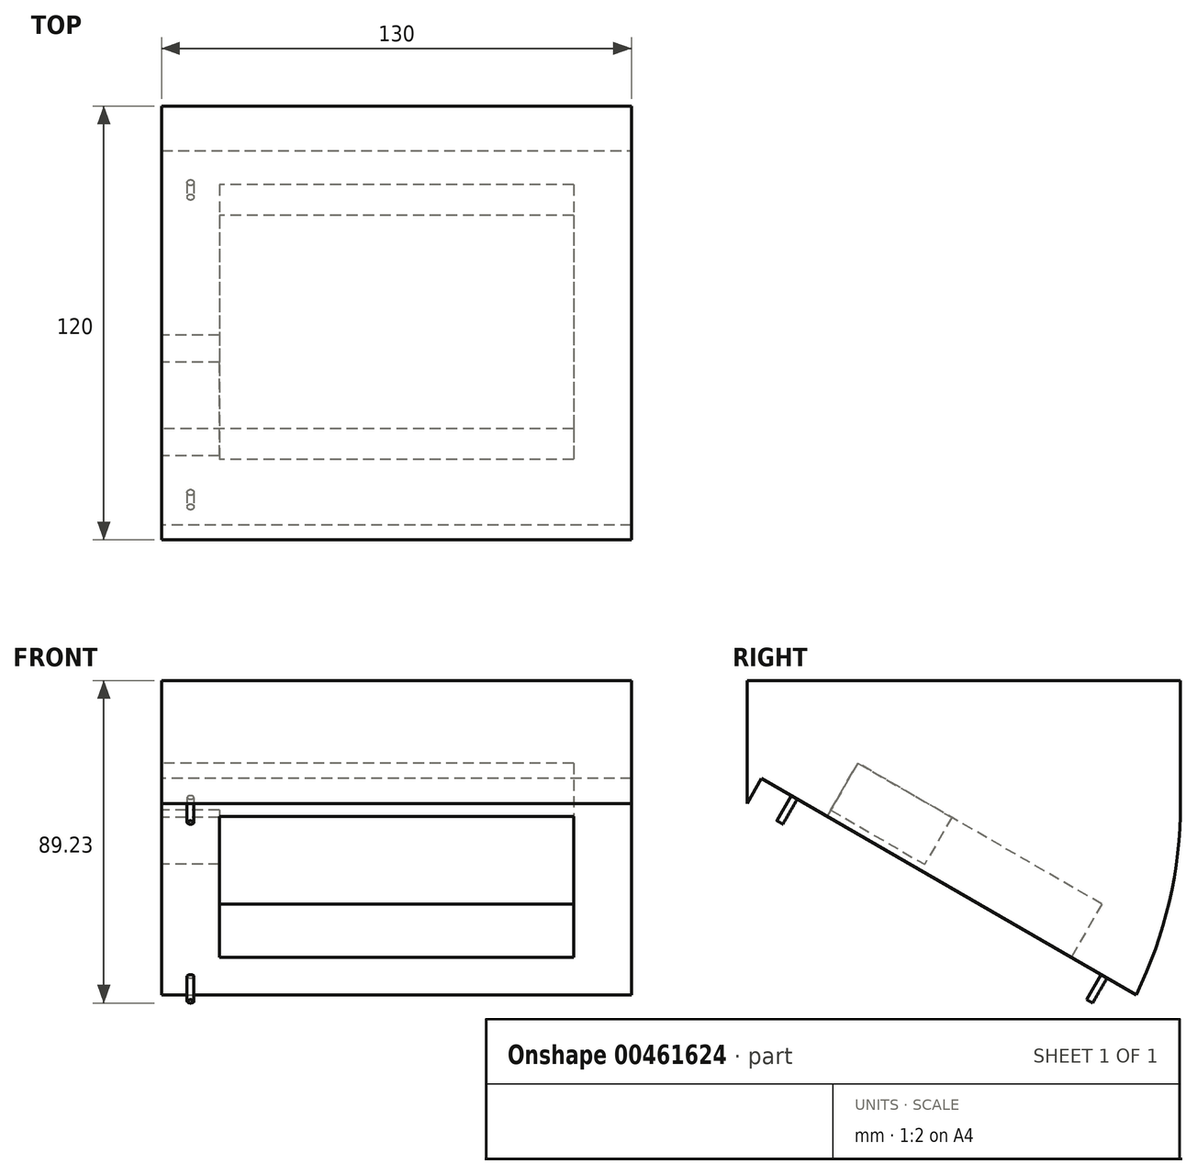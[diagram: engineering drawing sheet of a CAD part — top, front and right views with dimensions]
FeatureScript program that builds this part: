
annotation { "Feature Type Name" : "Feature", "Feature Type Description" : "" }
export const myFeature = defineFeature(function(context is Context, id is Id, definition is map)
    precondition{}
    {
        {
            var Q0;
            Q0=qCreatedBy(makeId("Top.planeOp"),FACE);
            var sketch = newSketch(context, id + "F0", { "sketchPlane" : qUnion([Q0])});
            skLineSegment(sketch, "E0.bottom", {"start": v(65, 60) * mm, "end": v(-65, 60) * mm});
            skLineSegment(sketch, "E0.top", {"start": v(65, -60) * mm, "end": v(-65, -60) * mm});
            skLineSegment(sketch, "E0.left", {"start": v(65, 60) * mm, "end": v(65, -60) * mm});
            skLineSegment(sketch, "E0.right", {"start": v(-65, 60) * mm, "end": v(-65, -60) * mm});
            skPoint(sketch, "E0.middle", {"position": v(0, 0) * mm});
            skSolve(sketch);
        }
        {
            var Q0;
            Q0=makeQuery(id+"F0.imprint","IMPRINT",FACE,{"disambiguationData":[TD([[makeQuery(id+"F0.imprint","IMPRINT",EDGE,{"derivedFrom":sQuery(id+"F0.wireOp",EDGE,"E0.bottom")}),1.0]])]});
            extrude(context, id + "F1", {"entities" : qUnion([Q0]), "depth" : 34 * mm, "offsetDistance" : 25 * mm});
        }
        {
            var Q0;
            Q0=makeQuery(id+"F0.imprint","IMPRINT",FACE,{"disambiguationData":[TD([[makeQuery(id+"F0.imprint","IMPRINT",EDGE,{"derivedFrom":sQuery(id+"F0.wireOp",EDGE,"E0.bottom")}),1.0]])]});
            var Q1;
            Q1=sQuery(id+"F0.wireOp",EDGE,"E0.top");
            revolve(context, id + "F2", {"operationType" : NewBodyOperationType.ADD, "entities" : qUnion([Q0]), "axis" : qUnion([Q1]), "revolveType" : RevolveType.ONE_DIRECTION, "angle" : 30 * degree});
        }
        {
            var Q0;
            Q0=makeQuery(id+"F2.opRevolve","CAP_FACE",FACE,{"disambiguationData":[OSD([sQuery(id+"F0.wireOp",EDGE,"E0.bottom"),sQuery(id+"F0.wireOp",EDGE,"E0.top"),sQuery(id+"F0.wireOp",EDGE,"E0.left"),sQuery(id+"F0.wireOp",EDGE,"E0.right")])],"isStart":false});
            var sketch = newSketch(context, id + "F3", { "sketchPlane" : qUnion([Q0])});
            skLineSegment(sketch, "E1", {"start": v(65, -68.04) * mm, "end": v(-65, 51.96) * mm, "construction": true});
            skLineSegment(sketch, "E2", {"start": v(-65, -68.04) * mm, "end": v(65, 51.96) * mm, "construction": true});
            skLineSegment(sketch, "E3.bottom", {"start": v(49, -47.04) * mm, "end": v(-49, -47.04) * mm});
            skLineSegment(sketch, "E3.top", {"start": v(49, 30.96) * mm, "end": v(-49, 30.96) * mm});
            skLineSegment(sketch, "E3.left", {"start": v(49, -47.04) * mm, "end": v(49, 30.96) * mm});
            skLineSegment(sketch, "E3.right", {"start": v(-49, -47.04) * mm, "end": v(-49, 30.96) * mm});
            skPoint(sketch, "E3.middle", {"position": v(0, -8.04) * mm});
            skSolve(sketch);
        }
        {
            var Q0;
            Q0=makeQuery(id+"F3.imprint","IMPRINT",FACE,{"disambiguationData":[TD([[makeQuery(id+"F3.imprint","IMPRINT",EDGE,{"derivedFrom":sQuery(id+"F3.wireOp",EDGE,"E3.bottom")}),-1.0]])]});
            extrude(context, id + "F4", {"entities" : qUnion([Q0]), "operationType" : NewBodyOperationType.REMOVE, "oppositeDirection" : true, "depth" : 25 * mm, "offsetDistance" : 25 * mm});
        }
        {
            var Q0;
            {var subQ0=sQuery(id+"F0.wireOp",EDGE,"E0.right");Q0=makeQuery(id+"F2.boolean.opBoolean","MERGE",FACE,{"derivedFrom":[makeQuery(id+"F1.opExtrude","SWEPT_FACE",FACE,{"disambiguationData":[OSD([subQ0])]}),makeQuery(id+"F2.opRevolve","SWEPT_FACE",FACE,{"disambiguationData":[OSD([subQ0])]})]});}
            var sketch = newSketch(context, id + "F5", { "sketchPlane" : qUnion([Q0])});
            skLineSegment(sketch, "E4", {"start": v(60, 0) * mm, "end": v(41.81, -10.5) * mm, "construction": true});
            skLineSegment(sketch, "E5", {"start": v(41.81, -10.5) * mm, "end": v(36.81, -1.84) * mm, "construction": true});
            skLineSegment(sketch, "E6", {"start": v(36.81, -1.84) * mm, "end": v(10.83, -16.84) * mm, "construction": true});
            skLineSegment(sketch, "E7", {"start": v(36.81, -1.84) * mm, "end": v(10.83, -16.84) * mm});
            skLineSegment(sketch, "E8", {"start": v(36.81, -1.84) * mm, "end": v(29.31, 11.15) * mm});
            skLineSegment(sketch, "E9", {"start": v(29.31, 11.15) * mm, "end": v(3.33, -3.85) * mm});
            skLineSegment(sketch, "E10", {"start": v(3.33, -3.85) * mm, "end": v(10.83, -16.84) * mm});
            skSolve(sketch);
        }
        {
            var Q0;
            Q0=makeQuery(id+"F5.imprint","IMPRINT",FACE,{"disambiguationData":[TD([[makeQuery(id+"F5.imprint","IMPRINT",EDGE,{"derivedFrom":sQuery(id+"F5.wireOp",EDGE,"E7")}),-1.0]])]});
            extrude(context, id + "F6", {"entities" : qUnion([Q0]), "operationType" : NewBodyOperationType.REMOVE, "oppositeDirection" : true, "depth" : 16 * mm, "offsetDistance" : 25 * mm});
        }
        {
            var Q0;
            Q0=makeQuery(id+"F2.opRevolve","CAP_FACE",FACE,{"disambiguationData":[OSD([sQuery(id+"F0.wireOp",EDGE,"E0.bottom"),sQuery(id+"F0.wireOp",EDGE,"E0.top"),sQuery(id+"F0.wireOp",EDGE,"E0.left"),sQuery(id+"F0.wireOp",EDGE,"E0.right")])],"isStart":false});
            var sketch = newSketch(context, id + "F7", { "sketchPlane" : qUnion([Q0])});
            skLineSegment(sketch, "E11", {"start": v(65, -68.04) * mm, "end": v(57, -68.04) * mm, "construction": true});
            skLineSegment(sketch, "E12", {"start": v(57, -68.04) * mm, "end": v(57, -57.54) * mm, "construction": true});
            skCircle(sketch, "E13", {"center": v(57, -57.54) * mm, "radius": 0.95 * mm});
            skLineSegment(sketch, "E14", {"start": v(65, 51.96) * mm, "end": v(57, 51.96) * mm, "construction": true});
            skLineSegment(sketch, "E15", {"start": v(57, 51.96) * mm, "end": v(57, 41.46) * mm, "construction": true});
            skCircle(sketch, "E16", {"center": v(57, 41.46) * mm, "radius": 0.95 * mm});
            skLineSegment(sketch, "E17", {"start": v(0, -68.04) * mm, "end": v(0, 51.96) * mm, "construction": true});
            skCircle(sketch, "E18.MirrorC", {"center": v(-57, -57.54) * mm, "radius": 0.95 * mm});
            skCircle(sketch, "E19.MirrorC", {"center": v(-57, 41.46) * mm, "radius": 0.95 * mm});
            skSolve(sketch);
        }
        {
            var Q0;
            Q0=makeQuery(id+"F7.imprint","IMPRINT",FACE,{"disambiguationData":[TD([[makeQuery(id+"F7.imprint","IMPRINT",EDGE,{"derivedFrom":sQuery(id+"F7.wireOp",EDGE,"E16")}),1.0]])]});
            var Q1;
            Q1=makeQuery(id+"F7.imprint","IMPRINT",FACE,{"disambiguationData":[TD([[makeQuery(id+"F7.imprint","IMPRINT",EDGE,{"derivedFrom":sQuery(id+"F7.wireOp",EDGE,"E19.MirrorC")}),-1.0]])]});
            var Q2;
            Q2=makeQuery(id+"F7.imprint","IMPRINT",FACE,{"disambiguationData":[TD([[makeQuery(id+"F7.imprint","IMPRINT",EDGE,{"derivedFrom":sQuery(id+"F7.wireOp",EDGE,"E18.MirrorC")}),-1.0]])]});
            var Q3;
            Q3=makeQuery(id+"F7.imprint","IMPRINT",FACE,{"disambiguationData":[TD([[makeQuery(id+"F7.imprint","IMPRINT",EDGE,{"derivedFrom":sQuery(id+"F7.wireOp",EDGE,"E13")}),1.0]])]});
            var Q4;
            Q4=sQuery(id+"F7.wireOp",EDGE,"E16");
            var Q5;
            Q5=sQuery(id+"F7.wireOp",EDGE,"E18.MirrorC");
            var Q6;
            Q6=sQuery(id+"F7.wireOp",EDGE,"E19.MirrorC");
            var Q7;
            Q7=sQuery(id+"F7.wireOp",EDGE,"E13");
            extrude(context, id + "F8", {"entities" : qUnion([Q0, Q1, Q2, Q3]), "operationType" : NewBodyOperationType.REMOVE, "surfaceEntities" : qUnion([Q4, Q5, Q6, Q7]), "oppositeDirection" : true, "depth" : 8 * mm, "offsetDistance" : 25 * mm});
        }
    });
